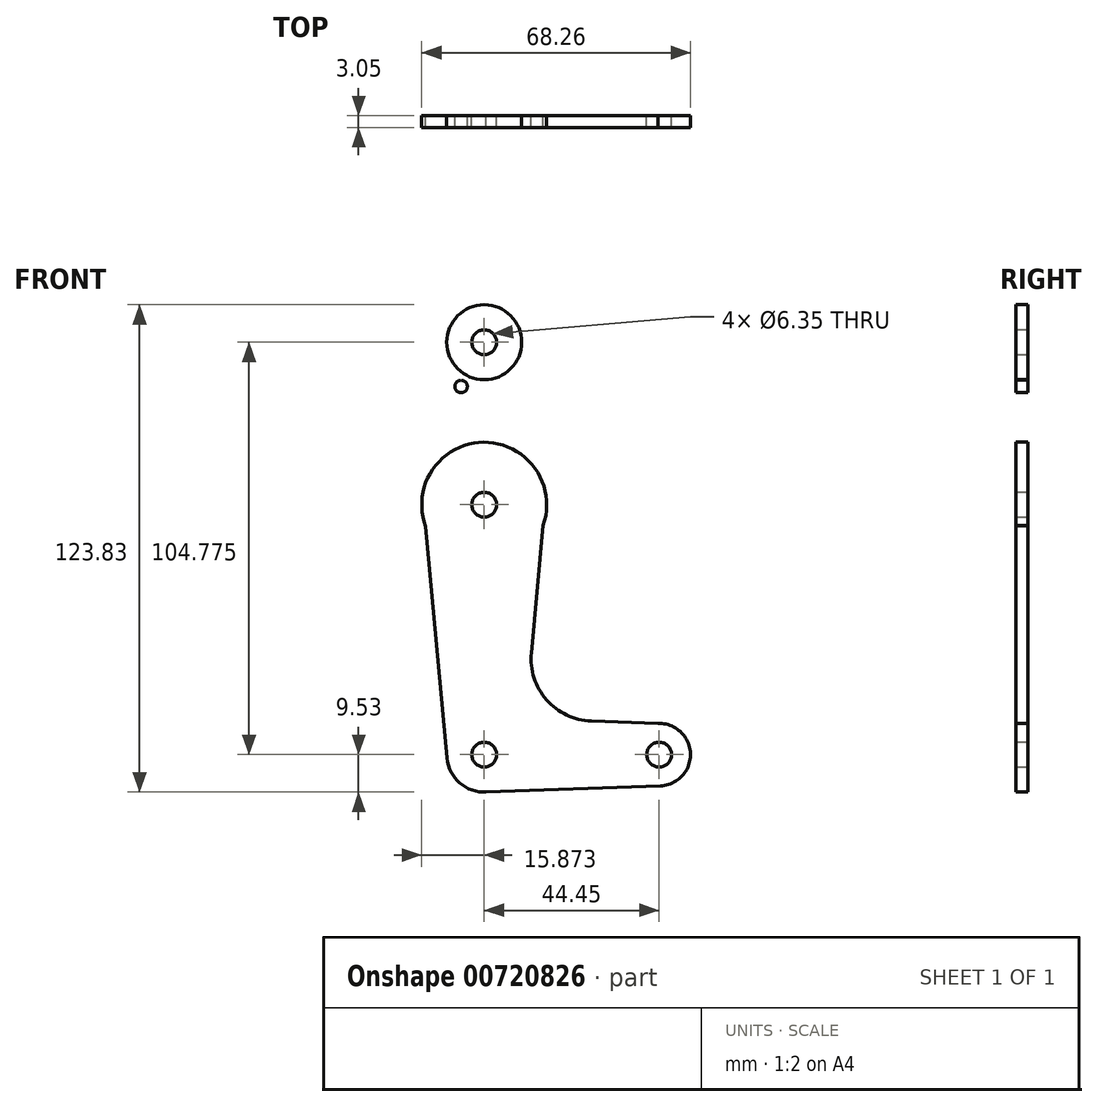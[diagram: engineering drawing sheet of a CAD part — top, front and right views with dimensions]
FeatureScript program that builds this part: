
annotation { "Feature Type Name" : "Feature", "Feature Type Description" : "" }
export const myFeature = defineFeature(function(context is Context, id is Id, definition is map)
    precondition{}
    {
        {
            var Q0;
            Q0=qCreatedBy(makeId("Front.planeOp"),FACE);
            var sketch = newSketch(context, id + "F0", { "sketchPlane" : qUnion([Q0])});
            skLineSegment(sketch, "E0", {"start": v(-336.52, 4.02) * mm, "end": v(-336.52, -100.75) * mm, "construction": true});
            skLineSegment(sketch, "E1", {"start": v(-336.52, -100.75) * mm, "end": v(-292.07, -100.75) * mm, "construction": true});
            skCircle(sketch, "E2", {"center": v(-336.52, 4.02) * mm, "radius": 9.53 * mm});
            skCircle(sketch, "E3", {"center": v(-336.52, -37.25) * mm, "radius": 15.88 * mm});
            skCircle(sketch, "E4", {"center": v(-336.52, -100.75) * mm, "radius": 9.53 * mm});
            skCircle(sketch, "E5", {"center": v(-292.07, -100.75) * mm, "radius": 7.94 * mm});
            skLineSegment(sketch, "E6", {"start": v(-344.4, 9.36) * mm, "end": v(-352.15, -34.49) * mm});
            skLineSegment(sketch, "E7", {"start": v(-352.15, -34.49) * mm, "end": v(-346, -101.62) * mm});
            skLineSegment(sketch, "E8", {"start": v(-328.53, 9.2) * mm, "end": v(-320.88, -34.49) * mm});
            skLineSegment(sketch, "E9", {"start": v(-320.82, -34.9) * mm, "end": v(-324.57, -74.86) * mm});
            skLineSegment(sketch, "E10", {"start": v(-291.12, -92.87) * mm, "end": v(-309.34, -92.2) * mm});
            skLineSegment(sketch, "E11", {"start": v(-336.34, -110.27) * mm, "end": v(-291.78, -108.68) * mm});
            skCircle(sketch, "E12", {"center": v(-336.52, 4.02) * mm, "radius": 3.18 * mm});
            skCircle(sketch, "E13", {"center": v(-342.39, -7.22) * mm, "radius": 1.59 * mm});
            skCircle(sketch, "E14", {"center": v(-336.52, -37.25) * mm, "radius": 3.18 * mm});
            skCircle(sketch, "E15", {"center": v(-336.52, -100.75) * mm, "radius": 3.18 * mm});
            skCircle(sketch, "E16", {"center": v(-292.07, -100.75) * mm, "radius": 3.18 * mm});
            skArc(sketch, "E17.filletArc", {"start": v(-324.57, -74.86) * mm, "mid": v(-320.69, -86.82) * mm, "end": v(-309.34, -92.2) * mm});
            skSolve(sketch);
        }
        {
            var Q0;
            Q0 = qSketchRegion(id + "F0", true);
            extrude(context, id + "F1", {"entities" : qUnion([Q0]), "depth" : 3.05 * mm, "offsetDistance" : 25.4 * mm});
        }
    });
